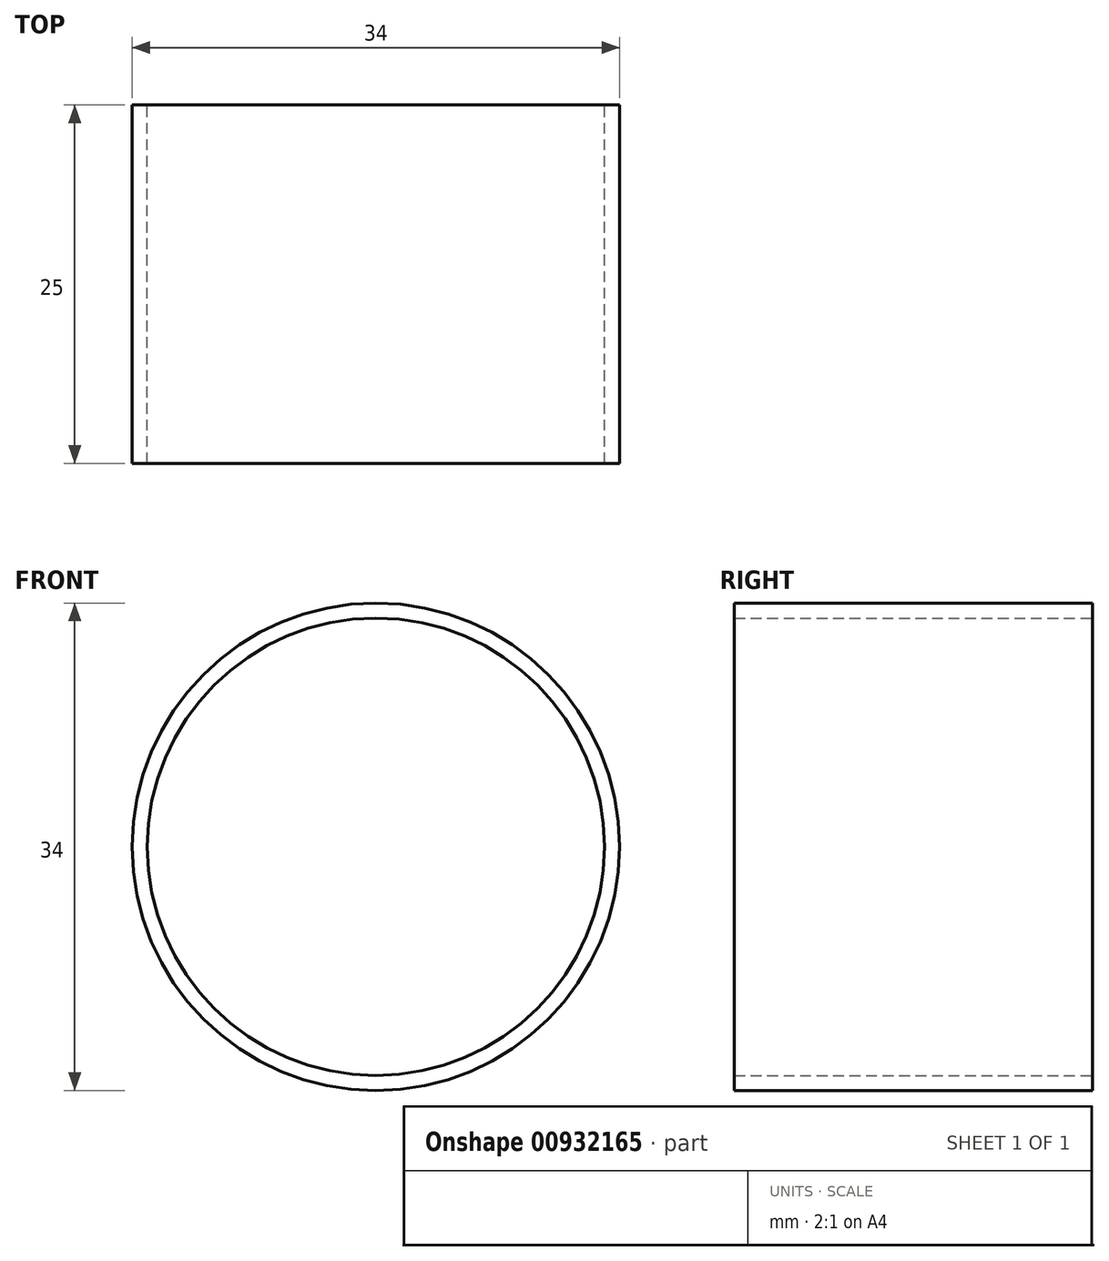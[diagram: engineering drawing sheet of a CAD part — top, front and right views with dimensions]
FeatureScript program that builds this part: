
annotation { "Feature Type Name" : "Feature", "Feature Type Description" : "" }
export const myFeature = defineFeature(function(context is Context, id is Id, definition is map)
    precondition{}
    {
        {
            var Q0;
            Q0=qCreatedBy(makeId("Front.planeOp"),FACE);
            var sketch = newSketch(context, id + "F0", { "sketchPlane" : qUnion([Q0])});
            skCircle(sketch, "E0", {"center": v(0, 0) * mm, "radius": 15.95 * mm});
            skCircle(sketch, "E1", {"center": v(0, 0) * mm, "radius": 17 * mm});
            skSolve(sketch);
        }
        {
            var Q0;
            Q0=makeQuery(id+"F0.imprint","IMPRINT",FACE,{"disambiguationData":[TD([[makeQuery(id+"F0.imprint","IMPRINT",EDGE,{"derivedFrom":sQuery(id+"F0.wireOp",EDGE,"E0")}),-1.0]])]});
            extrude(context, id + "F1", {"entities" : qUnion([Q0]), "depth" : 25 * mm, "offsetDistance" : 25 * mm});
        }
    });
